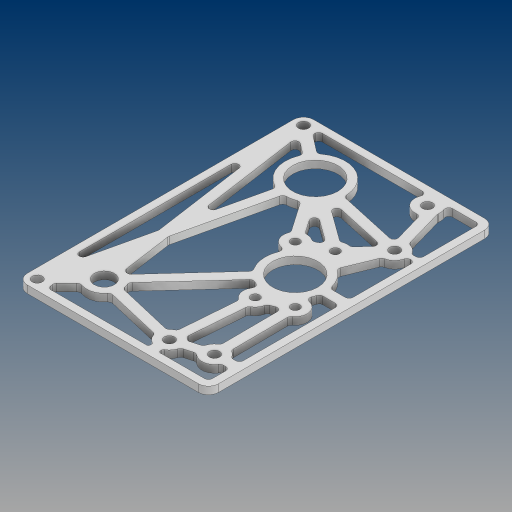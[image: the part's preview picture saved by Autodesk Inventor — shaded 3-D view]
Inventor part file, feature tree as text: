
AUTODESK INVENTOR PART (.ipt)
format: ipt  version: 2024.3 (Build 283343000, 343)  size: 683,008 bytes
history: native  units: in
note: dims shown in document units (in); Inventor stores cm internally (conversion verified against a paired STEP export)
features: extrude x3, sketch x2, projected_geometry x1
ambient origin geometry x8: Origin, YZ Plane, XZ Plane, XY Plane, X Axis, Y Axis, Z Axis, Center Point
bodies: Body1 (feature_tree)
feature tree (6):
  sketch  "Sketch1"  dims[d1=1.125in d2=0.5in]
  extrude  "Extrusion2"  Depth=0.5in
  extrude  "Extrusion5"  Depth=0.093in
  extrude  "Extrusion6"  Depth=0.093in
  sketch  "Sketch6"  dims[d4=0.5in d5=0.5in d6=0.256in d7=0.256in d8=0.5in d9=0.5in d17=2.44in d18=2.44in d19=2.0in d20=0.22in d21=3.1496in d23=360.0deg d25=1.125in d26=1.8in d27=1.8in d31=0.188in d32=0.256in d33=0.5in d34=0.256in d35=0.5in d38=0.1875in d39=0.1875in d40=0.1875in d41=0.25in d42=0.25in d43=0.1875in d44=0.0in d134=0.256in d135=0.256in d136=0.5in d162=0.457in d163=3.3875in d165=6.7749in d166=0.6043in d167=4.5in d168=1.0in d169=0.0in d199=0.188in d200=0.1875in d201=0.1875in d202=0.1875in d203=0.1875in d204=0.188in d205=0.188in d206=0.188in d207=0.188in d208=0.188in d209=0.125in d210=0.125in d211=0.093in d212=0.093in d213=0.093in d217=0.125in d218=0.125in d219=0.125in d220=0.125in d223=0.125in d224=0.125in d225=0.125in d226=0.093in d227=0.093in d228=0.093in d229=0.093in d230=0.125in d231=0.125in d233=0.093in d234=0.093in d235=0.093in d236=0.125in d237=0.125in d238=0.125in d239=0.125in d240=0.093in d241=0.125in d243=0.125in d244=0.125in d245=0.093in d246=0.093in d247=0.125in d248=0.125in d249=0.125in d250=0.125in d251=0.093in d252=0.093in d253=0.093in d254=0.125in d256=0.125in d257=0.093in d258=0.093in d259=0.093in d260=0.093in d261=0.125in d262=0.1875in d263=0.125in d264=0.125in d265=0.125in d266=0.188in d267=0.093in d268=0.093in d269=0.125in d270=0.125in d271=0.125in d273=0.188in d274=0.093in d275=0.125in d276=0.188in d277=0.093in d278=0.093in d279=0.125in d280=0.125in d281=0.125in d282=0.093in d283=0.125in d284=0.125in d285=0.125in d286=0.093in d287=1.0in d288=0.0in d289=1.568in d290=1.568in]
  projected_geometry  "Projected Loop3"
